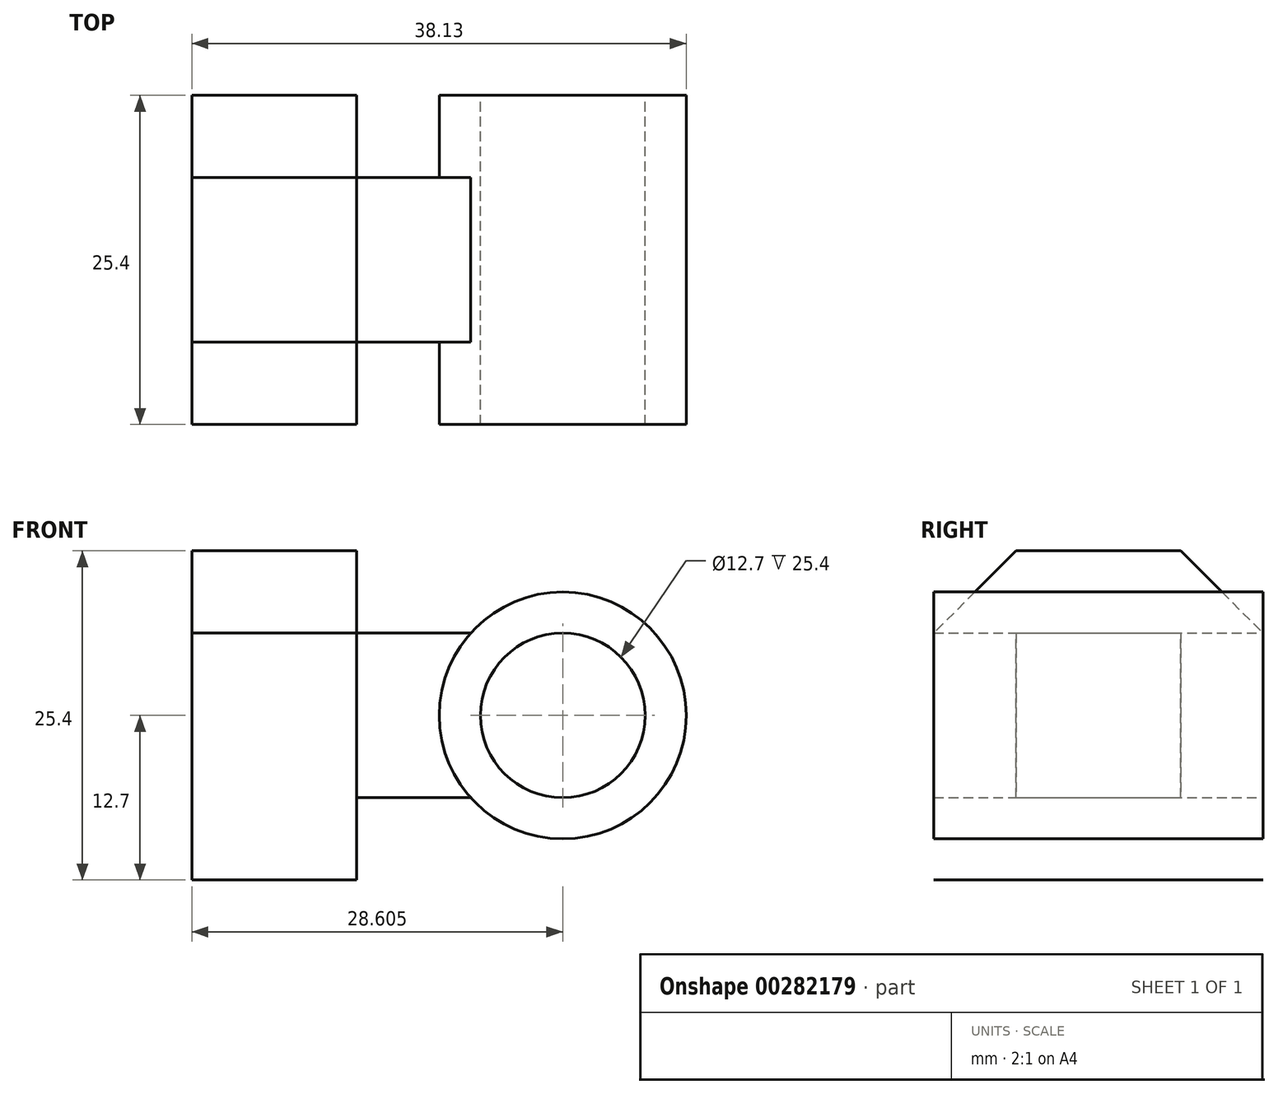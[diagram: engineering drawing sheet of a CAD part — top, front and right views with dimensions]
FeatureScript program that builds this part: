
annotation { "Feature Type Name" : "Feature", "Feature Type Description" : "" }
export const myFeature = defineFeature(function(context is Context, id is Id, definition is map)
    precondition{}
    {
        {
            var Q0;
            Q0=qCreatedBy(makeId("Top.planeOp"),FACE);
            var sketch = newSketch(context, id + "F0", { "sketchPlane" : qUnion([Q0])});
            skLineSegment(sketch, "E0", {"start": v(0, -12.7) * mm, "end": v(0, 12.7) * mm});
            skLineSegment(sketch, "E1", {"start": v(0, -12.7) * mm, "end": v(-12.7, -12.7) * mm});
            skLineSegment(sketch, "E2", {"start": v(-12.7, -12.7) * mm, "end": v(-12.7, 12.7) * mm});
            skLineSegment(sketch, "E3", {"start": v(-12.7, 12.7) * mm, "end": v(0, 12.7) * mm});
            skSolve(sketch);
        }
        {
            var Q0;
            Q0=makeQuery(id+"F0.imprint","IMPRINT",FACE,{"disambiguationData":[TD([[makeQuery(id+"F0.imprint","IMPRINT",EDGE,{"derivedFrom":sQuery(id+"F0.wireOp",EDGE,"E0")}),1.0]])]});
            extrude(context, id + "F1", {"entities" : qUnion([Q0]), "depth" : 25.4 * mm});
        }
        {
            var Q0;
            Q0=makeQuery(id+"F1.opExtrude","SWEPT_FACE",FACE,{"disambiguationData":[OSD([sQuery(id+"F0.wireOp",EDGE,"E0")])]});
            var sketch = newSketch(context, id + "F2", { "sketchPlane" : qUnion([Q0])});
            skLineSegment(sketch, "E4", {"start": v(-6.35, 25.4) * mm, "end": v(-12.7, 19.05) * mm});
            skLineSegment(sketch, "E5", {"start": v(-12.7, 19.05) * mm, "end": v(-12.7, 25.4) * mm});
            skLineSegment(sketch, "E6", {"start": v(-12.7, 25.4) * mm, "end": v(-6.35, 25.4) * mm});
            skSolve(sketch);
        }
        {
            var Q0;
            Q0=makeQuery(id+"F2.imprint","IMPRINT",FACE,{"disambiguationData":[TD([[makeQuery(id+"F2.imprint","IMPRINT",EDGE,{"derivedFrom":sQuery(id+"F2.wireOp",EDGE,"E4")}),-1.0]])]});
            extrude(context, id + "F3", {"entities" : qUnion([Q0]), "operationType" : NewBodyOperationType.REMOVE, "oppositeDirection" : true, "depth" : 25.4 * mm});
        }
        {
            var Q0;
            Q0=makeQuery(id+"F1.opExtrude","SWEPT_FACE",FACE,{"disambiguationData":[OSD([sQuery(id+"F0.wireOp",EDGE,"E0")])]});
            var sketch = newSketch(context, id + "F4", { "sketchPlane" : qUnion([Q0])});
            skLineSegment(sketch, "E7", {"start": v(6.35, 25.4) * mm, "end": v(12.7, 19.05) * mm});
            skLineSegment(sketch, "E8", {"start": v(12.7, 19.05) * mm, "end": v(12.7, 25.4) * mm});
            skLineSegment(sketch, "E9", {"start": v(12.7, 25.4) * mm, "end": v(6.35, 25.4) * mm});
            skSolve(sketch);
        }
        {
            var Q0;
            Q0=makeQuery(id+"F4.imprint","IMPRINT",FACE,{"disambiguationData":[TD([[makeQuery(id+"F4.imprint","IMPRINT",EDGE,{"derivedFrom":sQuery(id+"F4.wireOp",EDGE,"E7")}),1.0]])]});
            extrude(context, id + "F5", {"entities" : qUnion([Q0]), "operationType" : NewBodyOperationType.REMOVE, "oppositeDirection" : true, "depth" : 25.4 * mm});
        }
        {
            var Q0;
            Q0=makeQuery(id+"F1.opExtrude","SWEPT_FACE",FACE,{"disambiguationData":[OSD([sQuery(id+"F0.wireOp",EDGE,"E0")])]});
            var sketch = newSketch(context, id + "F6", { "sketchPlane" : qUnion([Q0])});
            skLineSegment(sketch, "E10", {"start": v(-6.35, 19.05) * mm, "end": v(6.35, 19.05) * mm});
            skLineSegment(sketch, "E11", {"start": v(6.35, 19.05) * mm, "end": v(6.35, 6.35) * mm});
            skLineSegment(sketch, "E12", {"start": v(6.35, 6.35) * mm, "end": v(-6.35, 6.35) * mm});
            skLineSegment(sketch, "E13", {"start": v(-6.35, 6.35) * mm, "end": v(-6.35, 19.05) * mm});
            skSolve(sketch);
        }
        {
            var Q0;
            Q0=makeQuery(id+"F6.imprint","IMPRINT",FACE,{"disambiguationData":[TD([[makeQuery(id+"F6.imprint","IMPRINT",EDGE,{"derivedFrom":sQuery(id+"F6.wireOp",EDGE,"E10")}),-1.0]])]});
            extrude(context, id + "F7", {"entities" : qUnion([Q0]), "operationType" : NewBodyOperationType.ADD, "depth" : 12.7 * mm});
        }
        {
            var Q0;
            Q0=qCreatedBy(makeId("Front.planeOp"),FACE);
            var sketch = newSketch(context, id + "F8", { "sketchPlane" : qUnion([Q0])});
            skCircle(sketch, "E14", {"center": v(15.9, 12.7) * mm, "radius": 9.53 * mm});
            skCircle(sketch, "E15", {"center": v(15.9, 12.7) * mm, "radius": 6.35 * mm});
            skSolve(sketch);
        }
        {
            var Q0;
            Q0=makeQuery(id+"F8.imprint","IMPRINT",FACE,{"disambiguationData":[TD([[makeQuery(id+"F8.imprint","IMPRINT",EDGE,{"derivedFrom":sQuery(id+"F8.wireOp",EDGE,"E14")}),1.0]])]});
            extrude(context, id + "F9", {"entities" : qUnion([Q0]), "depth" : 25.4 * mm, "symmetric" : true});
        }
        {
            var Q0;
            Q0=makeQuery(id+"F1.opExtrude","SWEPT_BODY",BODY,{"disambiguationData":[OSD([sQuery(id+"F0.wireOp",EDGE,"E0"),sQuery(id+"F0.wireOp",EDGE,"E1"),sQuery(id+"F0.wireOp",EDGE,"E2"),sQuery(id+"F0.wireOp",EDGE,"E3")])]});
            var Q1;
            Q1=makeQuery(id+"F9.opExtrude","SWEPT_BODY",BODY,{"disambiguationData":[OSD([sQuery(id+"F8.wireOp",EDGE,"E14"),sQuery(id+"F8.wireOp",EDGE,"E15")])]});
            booleanBodies(context, id + "F10", {"operationType" : BooleanOperationType.UNION, "tools" : qUnion([Q0, Q1])});
        }
        {
            var Q0;
            {var subQ0=sQuery(id+"F6.wireOp",EDGE,"E13");Q0=makeQuery(id+"F10.opBoolean","SPLIT",FACE,{"disambiguationData":[TD([makeQuery(id+"F9.opExtrude","SWEPT_FACE",FACE,{"disambiguationData":[OSD([sQuery(id+"F8.wireOp",EDGE,"E15")])]})])],"derivedFrom":makeQuery(id+"F7.opExtrude","SWEPT_FACE",FACE,{"disambiguationData":[OSD([subQ0])]})});}
            extrude(context, id + "F11", {"entities" : qUnion([Q0]), "operationType" : NewBodyOperationType.REMOVE, "oppositeDirection" : true, "depth" : 25.4 * mm});
        }
    });
